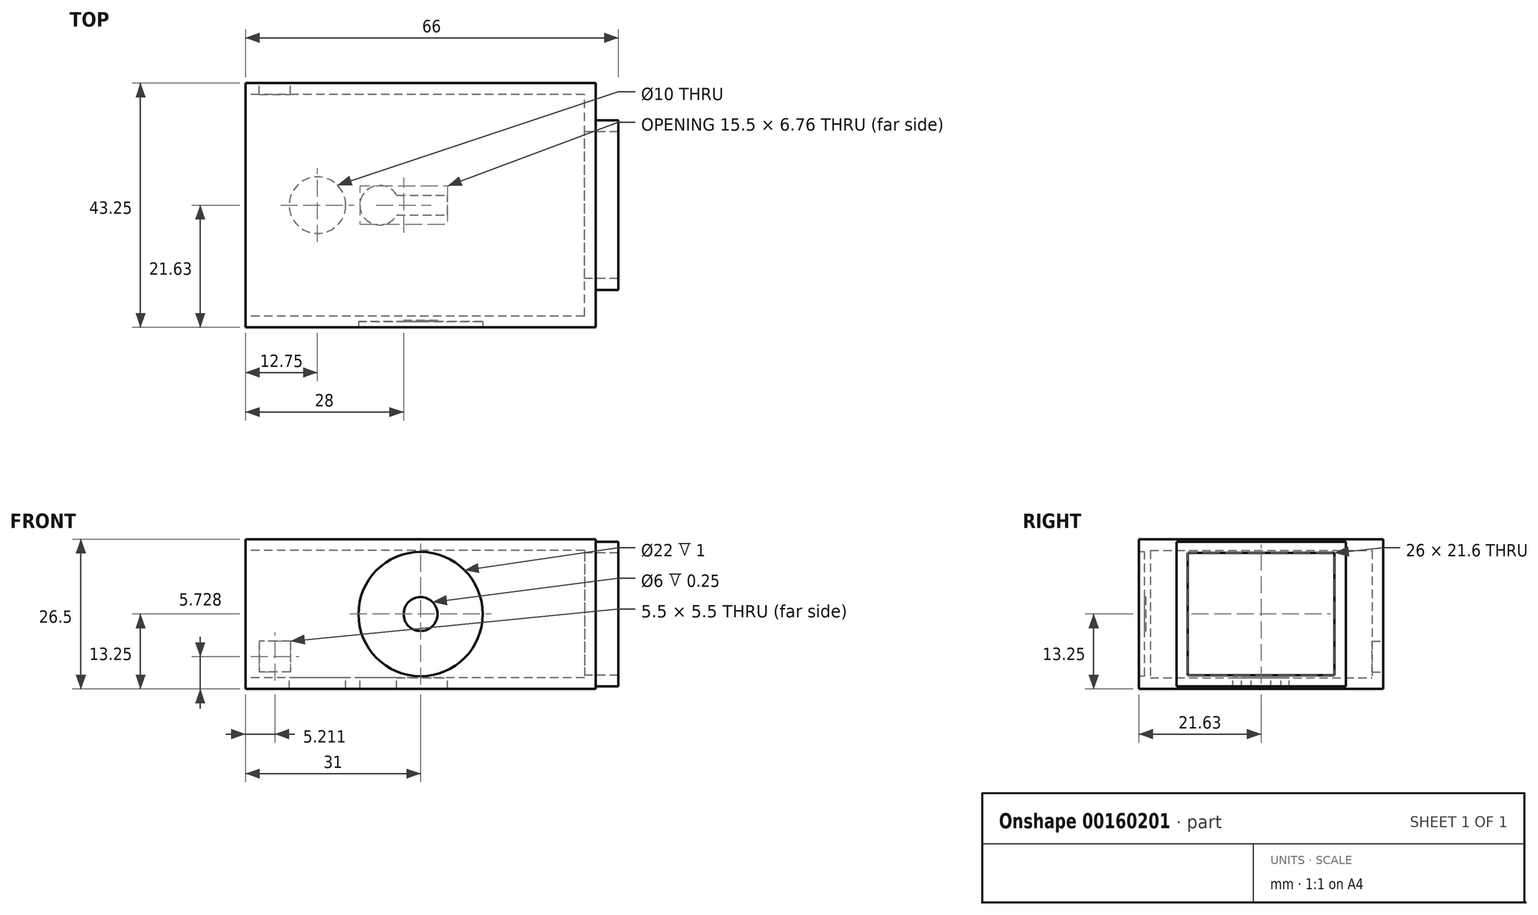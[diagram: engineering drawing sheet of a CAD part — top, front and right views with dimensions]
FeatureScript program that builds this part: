
annotation { "Feature Type Name" : "Feature", "Feature Type Description" : "" }
export const myFeature = defineFeature(function(context is Context, id is Id, definition is map)
    precondition{}
    {
        {
            var Q0;
            Q0=qCreatedBy(makeId("Top.planeOp"),FACE);
            var sketch = newSketch(context, id + "F0", { "sketchPlane" : qUnion([Q0])});
            skLineSegment(sketch, "E0.bottom", {"start": v(31, -21.63) * mm, "end": v(-31, -21.63) * mm});
            skLineSegment(sketch, "E0.top", {"start": v(31, 21.62) * mm, "end": v(-31, 21.63) * mm});
            skLineSegment(sketch, "E0.left", {"start": v(31, -21.63) * mm, "end": v(31, 21.63) * mm});
            skLineSegment(sketch, "E0.right", {"start": v(-31, -21.63) * mm, "end": v(-31, 21.63) * mm});
            skPoint(sketch, "E0.middle", {"position": v(0, 0) * mm});
            skPoint(sketch, "E1", {"position": v(35, 0) * mm});
            skLineSegment(sketch, "E2", {"start": v(35, -15) * mm, "end": v(35, 15) * mm});
            skLineSegment(sketch, "E3", {"start": v(35, 15) * mm, "end": v(31, 15) * mm});
            skLineSegment(sketch, "E4", {"start": v(35, -15) * mm, "end": v(31, -15) * mm});
            skLineSegment(sketch, "E5", {"start": v(31, -15) * mm, "end": v(31, -21.63) * mm});
            skLineSegment(sketch, "E6", {"start": v(-31, 0) * mm, "end": v(-18.25, 0) * mm});
            skPoint(sketch, "E6.endSnap0", {"position": v(-31, 0) * mm});
            skLineSegment(sketch, "E7", {"start": v(-31, 0) * mm, "end": v(-23, 0) * mm});
            skCircle(sketch, "E8", {"center": v(-18.25, 0) * mm, "radius": 5 * mm});
            skLineSegment(sketch, "E9", {"start": v(-13.25, 0) * mm, "end": v(-10.75, 0) * mm});
            skLineSegment(sketch, "E10", {"start": v(-13.25, 0) * mm, "end": v(-7.25, 0) * mm});
            skCircle(sketch, "E11", {"center": v(-7.25, 0) * mm, "radius": 3.5 * mm});
            skLineSegment(sketch, "E12", {"start": v(-7.25, 1.75) * mm, "end": v(4.75, 1.75) * mm});
            skLineSegment(sketch, "E13", {"start": v(-7.25, -1.75) * mm, "end": v(4.75, -1.75) * mm});
            skLineSegment(sketch, "E14", {"start": v(4.75, -1.75) * mm, "end": v(4.75, 1.75) * mm});
            skSolve(sketch);
        }
        {
            var Q0;
            {var subQ3=sQuery(id+"F0.wireOp",EDGE,"E0.bottom");Q0=makeQuery(id+"F0.imprint","IMPRINT",FACE,{"disambiguationData":[TD([[makeQuery(id+"F0.imprint","IMPRINT",EDGE,{"derivedFrom":subQ3}),-1.0]])]});}
            var Q1;
            {var subQ0=sQuery(id+"F0.wireOp",EDGE,"E8");var subQ1=makeQuery(id+"F0.imprint","IMPRINT",VERTEX,{"disambiguationData":[OD(0.0)],"derivedFrom":subQ0});Q1=makeQuery(id+"F0.imprint","IMPRINT",FACE,{"disambiguationData":[TD([[makeQuery(id+"F0.imprint","IMPRINT",EDGE,{"disambiguationData":[TD([[subQ1,-1.0]])],"derivedFrom":subQ0}),1.0]])]});}
            var Q2;
            {var subQ5=sQuery(id+"F0.wireOp",EDGE,"E14");Q2=makeQuery(id+"F0.imprint","IMPRINT",FACE,{"disambiguationData":[TD([[makeQuery(id+"F0.imprint","IMPRINT",EDGE,{"derivedFrom":subQ5}),1.0]])]});}
            var Q3;
            {var subQ0=sQuery(id+"F0.wireOp",EDGE,"E11");var subQ1=makeQuery(id+"F0.imprint","IMPRINT",VERTEX,{"derivedFrom":subQ0});Q3=makeQuery(id+"F0.imprint","IMPRINT",FACE,{"disambiguationData":[TD([[makeQuery(id+"F0.imprint","IMPRINT",EDGE,{"disambiguationData":[TD([[subQ1,1.0]])],"derivedFrom":subQ0}),1.0]])]});}
            extrude(context, id + "F1", {"entities" : qUnion([Q0, Q1, Q2, Q3]), "depth" : 13.25 * mm, "hasSecondDirection" : true, "secondDirectionOppositeDirection" : true, "secondDirectionDepth" : 13.25 * mm});
        }
        {
            var Q0;
            Q0=makeQuery(id+"F0.imprint","IMPRINT",FACE,{"disambiguationData":[TD([[makeQuery(id+"F0.imprint","IMPRINT",EDGE,{"derivedFrom":sQuery(id+"F0.wireOp",EDGE,"E2")}),1.0]])]});
            extrude(context, id + "F2", {"entities" : qUnion([Q0]), "operationType" : NewBodyOperationType.ADD, "depth" : 12.8 * mm, "hasSecondDirection" : true, "secondDirectionOppositeDirection" : true, "secondDirectionDepth" : 12.8 * mm});
        }
        {
            var Q0;
            Q0=makeQuery(id+"F2.opExtrude","SWEPT_FACE",FACE,{"disambiguationData":[OSD([sQuery(id+"F0.wireOp",EDGE,"E2")])]});
            var Q1;
            Q1=makeQuery(id+"F1.opExtrude","SWEPT_FACE",FACE,{"disambiguationData":[OSD([sQuery(id+"F0.wireOp",EDGE,"E0.right")])]});
            shell(context, id + "F3", {"entities" : qUnion([Q0, Q1]), "thickness" : 2 * mm});
        }
        {
            var Q0;
            Q0=makeQuery(id+"F1.opExtrude","SWEPT_FACE",FACE,{"disambiguationData":[OSD([sQuery(id+"F0.wireOp",EDGE,"E0.bottom")])]});
            cPlane(context, id + "F4", {"entities" : qUnion([Q0]), "cplaneType" : CPlaneType.OFFSET, "offset" : 0 * mm, "width" : 150 * mm, "height" : 150 * mm});
        }
        {
            var Q0;
            Q0=qCreatedBy(id+"F4.planeOp",FACE);
            var sketch = newSketch(context, id + "F5", { "sketchPlane" : qUnion([Q0])});
            skCircle(sketch, "E15", {"center": v(0, 0) * mm, "radius": 11 * mm});
            skCircle(sketch, "E16", {"center": v(0, 0) * mm, "radius": 3 * mm});
            skSolve(sketch);
        }
        {
            var Q0;
            Q0=makeQuery(id+"F5.imprint","IMPRINT",FACE,{"disambiguationData":[TD([[makeQuery(id+"F5.imprint","IMPRINT",EDGE,{"derivedFrom":sQuery(id+"F5.wireOp",EDGE,"E15")}),1.0]])]});
            extrude(context, id + "F6", {"entities" : qUnion([Q0]), "operationType" : NewBodyOperationType.REMOVE, "oppositeDirection" : true, "depth" : 1 * mm});
        }
        {
            var Q0;
            Q0=makeQuery(id+"F6.boolean.opBoolean","SPLIT",FACE,{"disambiguationData":[TD([makeQuery(id+"F6.opExtrude","SWEPT_FACE",FACE,{"disambiguationData":[OSD([sQuery(id+"F5.wireOp",EDGE,"E16")])]})])],"derivedFrom":makeQuery(id+"F1.opExtrude","SWEPT_FACE",FACE,{"disambiguationData":[OSD([sQuery(id+"F0.wireOp",EDGE,"E0.bottom")])]})});
            extrude(context, id + "F7", {"entities" : qUnion([Q0]), "operationType" : NewBodyOperationType.REMOVE, "oppositeDirection" : true, "depth" : 1.25 * mm});
        }
        {
            var Q0;
            {var subQ0=sQuery(id+"F0.wireOp",EDGE,"E8");var subQ1=makeQuery(id+"F0.imprint","IMPRINT",VERTEX,{"disambiguationData":[OD(0.0)],"derivedFrom":subQ0});Q0=makeQuery(id+"F0.imprint","IMPRINT",FACE,{"disambiguationData":[TD([[makeQuery(id+"F0.imprint","IMPRINT",EDGE,{"disambiguationData":[TD([[subQ1,-1.0]])],"derivedFrom":subQ0}),1.0]])]});}
            var Q1;
            {var subQ5=sQuery(id+"F0.wireOp",EDGE,"E14");Q1=makeQuery(id+"F0.imprint","IMPRINT",FACE,{"disambiguationData":[TD([[makeQuery(id+"F0.imprint","IMPRINT",EDGE,{"derivedFrom":subQ5}),1.0]])]});}
            var Q2;
            {var subQ0=sQuery(id+"F0.wireOp",EDGE,"E11");var subQ1=makeQuery(id+"F0.imprint","IMPRINT",VERTEX,{"derivedFrom":subQ0});Q2=makeQuery(id+"F0.imprint","IMPRINT",FACE,{"disambiguationData":[TD([[makeQuery(id+"F0.imprint","IMPRINT",EDGE,{"disambiguationData":[TD([[subQ1,1.0]])],"derivedFrom":subQ0}),1.0]])]});}
            extrude(context, id + "F8", {"entities" : qUnion([Q0, Q1, Q2]), "operationType" : NewBodyOperationType.REMOVE, "oppositeDirection" : true, "depth" : 25 * mm});
        }
        {
            var Q0;
            Q0=makeQuery(id+"F1.opExtrude","SWEPT_FACE",FACE,{"disambiguationData":[OSD([sQuery(id+"F0.wireOp",EDGE,"E0.top")])]});
            cPlane(context, id + "F9", {"entities" : qUnion([Q0]), "cplaneType" : CPlaneType.OFFSET, "offset" : 0 * mm, "width" : 150 * mm, "height" : 150 * mm});
        }
        {
            var Q0;
            Q0=qCreatedBy(id+"F9.planeOp",FACE);
            var sketch = newSketch(context, id + "F10", { "sketchPlane" : qUnion([Q0])});
            skLineSegment(sketch, "E17.bottom", {"start": v(23.04, -4.77) * mm, "end": v(28.54, -4.77) * mm});
            skLineSegment(sketch, "E17.top", {"start": v(23.04, -10.27) * mm, "end": v(28.54, -10.27) * mm});
            skLineSegment(sketch, "E17.left", {"start": v(23.04, -4.77) * mm, "end": v(23.04, -10.27) * mm});
            skLineSegment(sketch, "E17.right", {"start": v(28.54, -4.77) * mm, "end": v(28.54, -10.27) * mm});
            skSolve(sketch);
        }
        {
            var Q0;
            Q0=makeQuery(id+"F10.imprint","IMPRINT",FACE,{"disambiguationData":[TD([[makeQuery(id+"F10.imprint","IMPRINT",EDGE,{"derivedFrom":sQuery(id+"F10.wireOp",EDGE,"E17.bottom")}),-1.0]])]});
            var Q1;
            Q1=sQuery(id+"F10.wireOp",EDGE,"E17.top");
            var Q2;
            Q2=sQuery(id+"F10.wireOp",EDGE,"E17.left");
            var Q3;
            Q3=sQuery(id+"F10.wireOp",EDGE,"E17.right");
            var Q4;
            Q4=sQuery(id+"F10.wireOp",EDGE,"E17.bottom");
            extrude(context, id + "F11", {"entities" : qUnion([Q0]), "operationType" : NewBodyOperationType.REMOVE, "surfaceEntities" : qUnion([Q1, Q2, Q3, Q4]), "oppositeDirection" : true, "depth" : 25 * mm});
        }
    });
